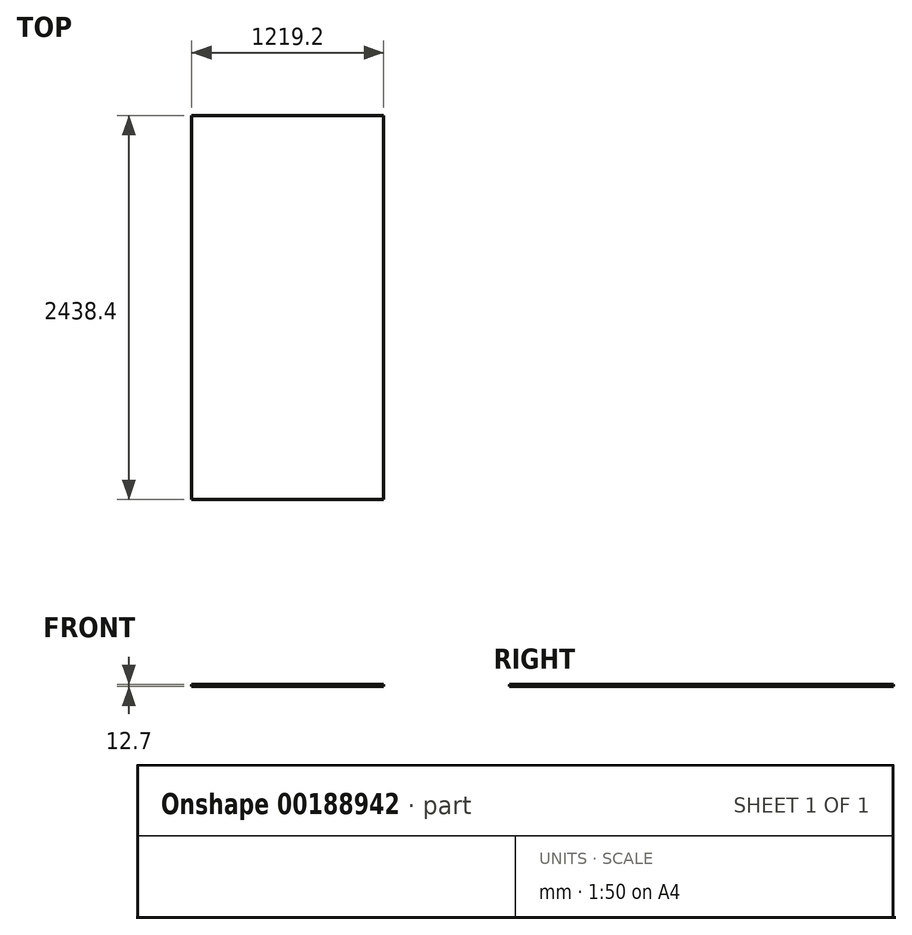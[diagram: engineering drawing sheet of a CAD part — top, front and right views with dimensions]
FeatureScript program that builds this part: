
annotation { "Feature Type Name" : "Feature", "Feature Type Description" : "" }
export const myFeature = defineFeature(function(context is Context, id is Id, definition is map)
    precondition{}
    {
        {
            var Q0;
            Q0=qCreatedBy(makeId("Top.planeOp"),FACE);
            var sketch = newSketch(context, id + "F1", { "sketchPlane" : qUnion([Q0])});
            skLineSegment(sketch, "E0.bottom", {"start": v(609.6, -1219.2) * mm, "end": v(-609.6, -1219.2) * mm});
            skLineSegment(sketch, "E0.top", {"start": v(609.6, 1219.2) * mm, "end": v(-609.6, 1219.2) * mm});
            skLineSegment(sketch, "E0.left", {"start": v(609.6, -1219.2) * mm, "end": v(609.6, 1219.2) * mm});
            skLineSegment(sketch, "E0.right", {"start": v(-609.6, -1219.2) * mm, "end": v(-609.6, 1219.2) * mm});
            skPoint(sketch, "E0.middle", {"position": v(0, 0) * mm});
            skSolve(sketch);
        }
        {
            var Q0;
            Q0=makeQuery(id+"F1.imprint","IMPRINT",FACE,{"disambiguationData":[TD([[makeQuery(id+"F1.imprint","IMPRINT",EDGE,{"derivedFrom":sQuery(id+"F1.wireOp",EDGE,"E0.bottom")}),-1.0]])]});
            extrude(context, id + "F0", {"entities" : qUnion([Q0]), "endBound" : BoundingType.SYMMETRIC, "depth" : 12.7 * mm});
        }
    });
